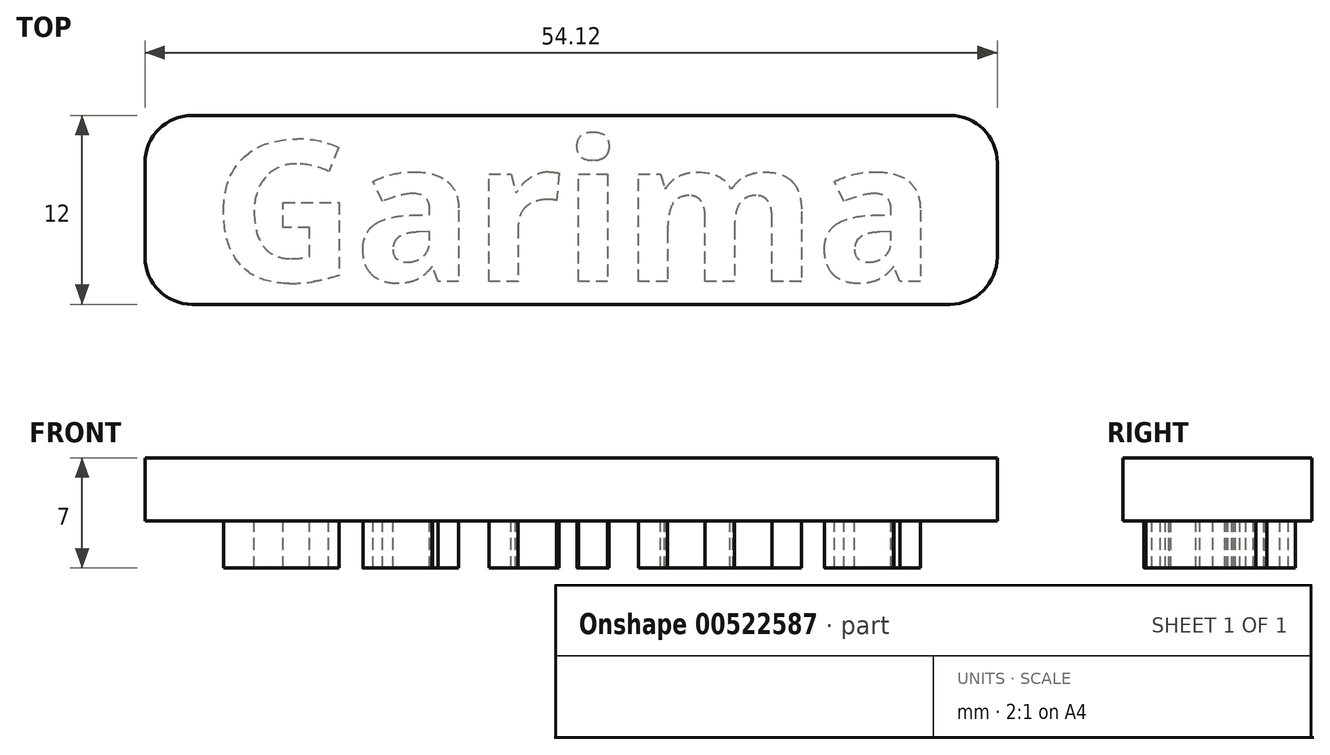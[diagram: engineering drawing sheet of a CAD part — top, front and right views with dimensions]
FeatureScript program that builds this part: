
annotation { "Feature Type Name" : "Feature", "Feature Type Description" : "" }
export const myFeature = defineFeature(function(context is Context, id is Id, definition is map)
    precondition{}
    {
        {
            var Q0;
            Q0=qCreatedBy(makeId("Top.planeOp"),FACE);
            var sketch = newSketch(context, id + "F0", { "sketchPlane" : qUnion([Q0])});
            skText(sketch, "E0", { "text": "Garima", "fontName": "OpenSans-Bold.ttf"});
            skPoint(sketch, "E1", {"position": v(0, 0) * mm});
            const initialGuessF0  = {"E0": [-0.0229, -0.0045, 1, 0, 0.009]};
            skSetInitialGuess(sketch, initialGuessF0);
            skSolve(sketch);
        }
        {
            var Q0;
            Q0=qCreatedBy(makeId("Top.planeOp"),FACE);
            var sketch = newSketch(context, id + "F1", { "sketchPlane" : qUnion([Q0])});
            skLineSegment(sketch, "E2.bottom", {"start": v(-27.16, 6.05) * mm, "end": v(26.96, 6.05) * mm});
            skLineSegment(sketch, "E2.top", {"start": v(-27.16, -5.95) * mm, "end": v(26.96, -5.95) * mm});
            skLineSegment(sketch, "E2.left", {"start": v(-27.16, 6.05) * mm, "end": v(-27.16, -5.95) * mm});
            skLineSegment(sketch, "E2.right", {"start": v(26.96, 6.05) * mm, "end": v(26.96, -5.95) * mm});
            skSolve(sketch);
        }
        {
            var Q0;
            Q0=makeQuery(id+"F1.imprint","IMPRINT",FACE,{"disambiguationData":[TD([[makeQuery(id+"F1.imprint","IMPRINT",EDGE,{"derivedFrom":sQuery(id+"F1.wireOp",EDGE,"E2.bottom")}),-1.0]])]});
            extrude(context, id + "F2", {"entities" : qUnion([Q0]), "depth" : 4 * mm, "offsetDistance" : 25 * mm});
        }
        {
            var Q0;
            Q0 = qSketchRegion(id + "F0", true);
            extrude(context, id + "F3", {"entities" : qUnion([Q0]), "operationType" : NewBodyOperationType.ADD, "oppositeDirection" : true, "depth" : 3 * mm, "offsetDistance" : 25 * mm});
        }
        {
            var Q0;
            Q0=makeQuery(id+"F2.opExtrude","SWEPT_EDGE",EDGE,{"disambiguationData":[OSD([sQuery(id+"F1.wireOp",EDGE,"E2.bottom"),sQuery(id+"F1.wireOp",EDGE,"E2.left")])]});
            var Q1;
            Q1=makeQuery(id+"F2.opExtrude","SWEPT_EDGE",EDGE,{"disambiguationData":[OSD([sQuery(id+"F1.wireOp",EDGE,"E2.bottom"),sQuery(id+"F1.wireOp",EDGE,"E2.right")])]});
            var Q2;
            Q2=makeQuery(id+"F2.opExtrude","SWEPT_EDGE",EDGE,{"disambiguationData":[OSD([sQuery(id+"F1.wireOp",EDGE,"E2.top"),sQuery(id+"F1.wireOp",EDGE,"E2.right")])]});
            var Q3;
            Q3=makeQuery(id+"F2.opExtrude","SWEPT_EDGE",EDGE,{"disambiguationData":[OSD([sQuery(id+"F1.wireOp",EDGE,"E2.top"),sQuery(id+"F1.wireOp",EDGE,"E2.left")])]});
            fillet(context, id + "F4", {"entities" : qUnion([Q0, Q1, Q2, Q3]), "radius" : 3 * mm, "tangentPropagation" : true, "allowEdgeOverflow" : false});
        }
    });
